# Revit family: Robuust 500 SMART
name_source: partatom
category: Generic Models
revit_build: Autodesk Revit 2018 (Build: 20170223_1515(x64)
units: mm (PartAtom-declared; Revit-internal decimal feet)

## family parameters
Always vertical = Yes
Can host rebar = No
Cut with Voids When Loaded = No
Part Type = Normal
Room Calculation Point = No
Round Connector Dimension = Use Diameter
Shared = No
Work Plane-Based = No

## types (1)
- Robuust 500 SMART
    Art. No. = 430 750 500
    Bedienings knoppen = Grijs kunststof reflective
    Bedieningspaneel = Kunststof grijs mat
    Breedte = 530 mm  [stored 1.73885 ft]
    Diepte = 118 mm  [stored 0.387139 ft]
    Hoogte = 450 mm  [stored 1.47638 ft]
    Lacquer = Lacquer White
    Manufacturer = Masterwatt B.V.
    Model = Robuust 500 SMART
    Phase = 1
    Power (default) = 500 VA
    Scherm = Scherm
    URL = https://masterwatt.nl
    Voltage = 230 V

note: [stored X ft] marks values corroborated as IEEE doubles in the binary element streams (Revit-internal decimal feet)

## geometry (parser evidence)
native form markers: Sweep x9
no freeform markers — native parametric forms only
